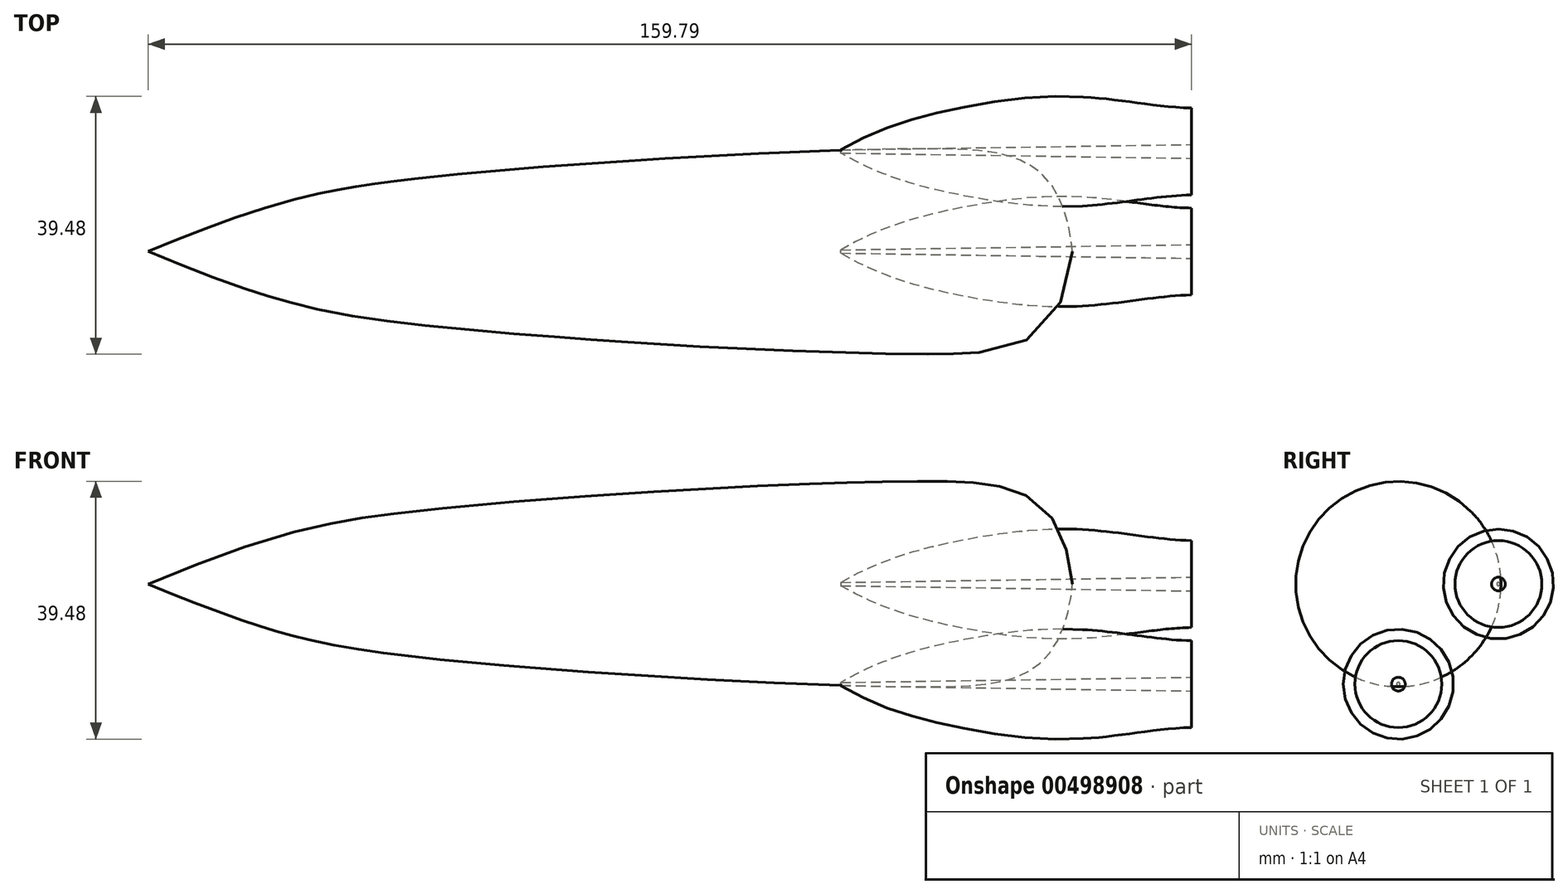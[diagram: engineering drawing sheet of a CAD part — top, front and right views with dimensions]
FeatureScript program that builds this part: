
annotation { "Feature Type Name" : "Feature", "Feature Type Description" : "" }
export const myFeature = defineFeature(function(context is Context, id is Id, definition is map)
    precondition{}
    {
        {
            var Q0;
            Q0=qCreatedBy(makeId("Top.planeOp"),FACE);
            var sketch = newSketch(context, id + "F0", { "sketchPlane" : qUnion([Q0])});
            skFitSpline(sketch, "E0", {"points": [v(-73.6, 0) * mm, v(-31.1, 11.32) * mm, v(45.9, 15.72) * mm, v(68.02, 0) * mm], "startDerivative": vector(180.78, 74.98) * mm, "endDerivative": vector(19.1, -177.26) * mm});
            skLineSegment(sketch, "E1", {"start": v(68.02, 0) * mm, "end": v(-73.6, 0) * mm});
            skSolve(sketch);
        }
        {
            var Q0;
            Q0=qCreatedBy(makeId("Top.planeOp"),FACE);
            var sketch = newSketch(context, id + "F1", { "sketchPlane" : qUnion([Q0])});
            skLineSegment(sketch, "E2", {"start": v(-84.5, 0) * mm, "end": v(68, 0) * mm});
            skSolve(sketch);
        }
        {
            var Q0;
            Q0=makeQuery(id+"F0.imprint","IMPRINT",FACE,{"disambiguationData":[TD([[makeQuery(id+"F0.imprint","IMPRINT",EDGE,{"derivedFrom":sQuery(id+"F0.wireOp",EDGE,"E0")}),-1.0]])]});
            var Q1;
            Q1=sQuery(id+"F0.wireOp",EDGE,"E0");
            var Q2;
            Q2=sQuery(id+"F1.wireOp",EDGE,"E2");
            revolve(context, id + "F2", {"entities" : qUnion([Q0]), "surfaceEntities" : qUnion([Q1]), "axis" : qUnion([Q2]), "revolveType" : RevolveType.FULL});
        }
        {
            var Q0;
            Q0=qCreatedBy(makeId("Top.planeOp"),FACE);
            var sketch = newSketch(context, id + "F3", { "sketchPlane" : qUnion([Q0])});
            skFitSpline(sketch, "E3", {"points": [v(32.5, 15.58) * mm, v(50.11, 21.88) * mm, v(69.08, 23.7) * mm, v(86.2, 21.98) * mm], "startDerivative": vector(50.54, 30.04) * mm, "endDerivative": vector(48.11, -0.83) * mm});
            skLineSegment(sketch, "E4", {"start": v(86.2, 21.98) * mm, "end": v(86.13, 16.38) * mm});
            skLineSegment(sketch, "E5", {"start": v(86.13, 16.38) * mm, "end": v(32.5, 15.58) * mm});
            skSolve(sketch);
        }
        {
            var Q0;
            Q0=qCreatedBy(makeId("Top.planeOp"),FACE);
            var sketch = newSketch(context, id + "F4", { "sketchPlane" : qUnion([Q0])});
            skLineSegment(sketch, "E6", {"start": v(28.2, 15.33) * mm, "end": v(87.18, 15.33) * mm});
            skSolve(sketch);
        }
        {
            var Q0;
            Q0=makeQuery(id+"F3.imprint","IMPRINT",FACE,{"disambiguationData":[TD([[makeQuery(id+"F3.imprint","IMPRINT",EDGE,{"derivedFrom":sQuery(id+"F3.wireOp",EDGE,"E3")}),-1.0]])]});
            var Q1;
            Q1=sQuery(id+"F3.wireOp",EDGE,"E3");
            var Q2;
            Q2=sQuery(id+"F4.wireOp",EDGE,"E6");
            revolve(context, id + "F5", {"entities" : qUnion([Q0]), "surfaceEntities" : qUnion([Q1]), "axis" : qUnion([Q2]), "revolveType" : RevolveType.FULL});
        }
        {
            var Q0;
            Q0=makeQuery(id+"FNVikcuDjCnMbcQ_1.1.F5.opRevolve","SWEPT_BODY",BODY,{"disambiguationData":[OSD([sQuery(id+"FNVikcuDjCnMbcQ_1.1.F3.wireOp",EDGE,"E3")])]});
            var Q1;
            Q1=makeQuery(id+"F5.opRevolve","SWEPT_BODY",BODY,{"disambiguationData":[OSD([sQuery(id+"F3.wireOp",EDGE,"E3")])]});
            var Q2;
            Q2=qCreatedBy(makeId("Front.planeOp"),FACE);
            mirror(context, id + "F6", {"entities" : qUnion([Q0, Q1]), "mirrorPlane" : qUnion([Q2])});
        }
        {
            var Q0;
            Q0=makeQuery(id+"F6.opPattern","COPY",BODY,{"derivedFrom":makeQuery(id+"F5.opRevolve","SWEPT_BODY",BODY,{"disambiguationData":[OSD([sQuery(id+"F3.wireOp",EDGE,"E3")])]}),"instanceName":"1"});
            var Q1;
            Q1=makeQuery(id+"F6.opPattern","COPY",BODY,{"derivedFrom":makeQuery(id+"FNVikcuDjCnMbcQ_1.1.F5.opRevolve","SWEPT_BODY",BODY,{"disambiguationData":[OSD([sQuery(id+"FNVikcuDjCnMbcQ_1.1.F3.wireOp",EDGE,"E3")])]}),"instanceName":"1"});
            var Q2;
            Q2=sQuery(id+"F1.wireOp",EDGE,"E2");
            transform(context, id + "F7", {"entities" : qUnion([Q0, Q1]), "transformType" : TransformType.ROTATION, "transformAxis" : qUnion([Q2]), "angle" : 90 * degree, "makeCopy" : false});
        }
        {
            var Q0;
            Q0=makeQuery(id+"F2.opRevolve","SWEPT_BODY",BODY,{"disambiguationData":[OSD([sQuery(id+"F0.wireOp",EDGE,"E0"),sQuery(id+"F0.wireOp",EDGE,"E1")])]});
            var Q1;
            Q1=sQuery(id+"F1.wireOp",EDGE,"E2");
            transform(context, id + "F8", {"entities" : qUnion([Q0]), "transformType" : TransformType.ROTATION, "transformAxis" : qUnion([Q1]), "angle" : 45 * degree, "makeCopy" : false});
        }
    });
